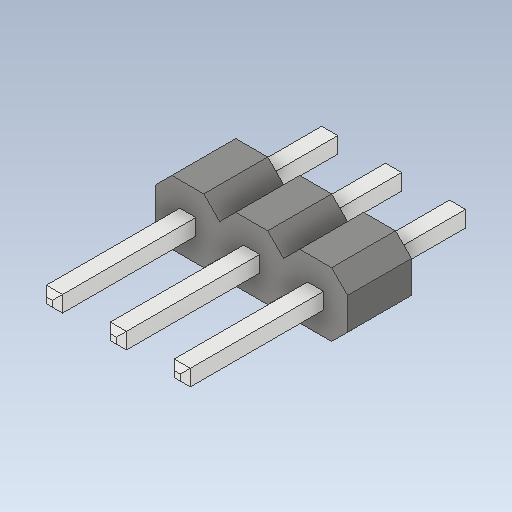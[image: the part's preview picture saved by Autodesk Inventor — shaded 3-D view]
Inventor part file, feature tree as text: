
AUTODESK INVENTOR PART (.ipt)
format: ipt  version: 2020 (Build 240168000, 168)  size: 142,336 bytes
history: imported  units: in
note: dims shown in document units (in); Inventor stores cm internally (conversion verified against a paired STEP export)
features: imported_body x1
ambient origin geometry x8: Origin, YZ Plane, XZ Plane, XY Plane, X Axis, Y Axis, Z Axis, Center Point
bodies: Solid1 (imported_parasolid), Body2 (imported_parasolid)
feature tree (1):
  imported_body  NMx_Import_Brep_tag  [imported B-rep: ~76 faces, bbox_mm=[7.62, 2.54, 11.34]]
